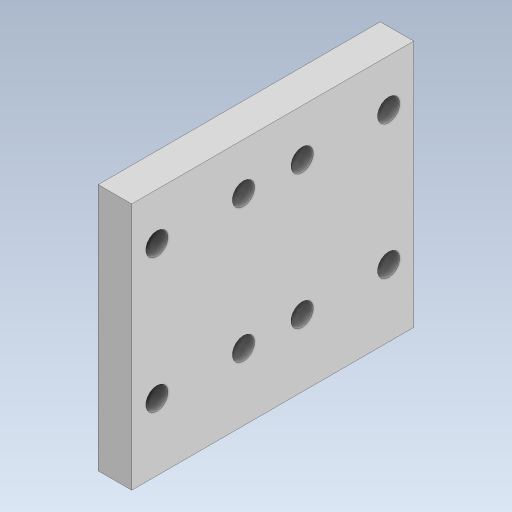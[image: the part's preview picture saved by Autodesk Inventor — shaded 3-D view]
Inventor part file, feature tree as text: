
AUTODESK INVENTOR PART (.ipt)
format: ipt  version: 2023.5 (Build 275446000, 446)  size: 292,864 bytes
history: native  units: in
note: dims shown in document units (in); Inventor stores cm internally (conversion verified against a paired STEP export)
features: extrude x2, sketch x1
ambient origin geometry x8: Origin, YZ Plane, XZ Plane, XY Plane, X Axis, Y Axis, Z Axis, Center Point
bodies: Solid1 (feature_tree)
feature tree (3):
  sketch  "Sketch1"  dims[d0=0.874in d1=0.9941in d2=0.0787in d3=0.2362in d4=0.0886in d5=0.0787in d6=0.3937in d9=0.0787in d10=0.1654in d12=0.1181in d13=0.0in d14=0.0787in d15=0.0787in d16=0.1181in d17=0.0in]
  extrude  "Extrusion1"  Depth=0.9941in
  extrude  "Extrusion2"  Depth=0.1181in
